# Revit family: Camera-Security-iPRO-Super_Dynamic-2MP_Vandal_Resistant_Outdoor_PTZ-_Network-WV-U65300-ZYX
name_source: partatom
category: Security Devices
units: mm (PartAtom-declared; Revit-internal decimal feet)

## family parameters
Cut with Voids When Loaded = No
Host = Face
Maintain Annotation Orientation = No
OmniClass Number = 23.85.10.14.11
OmniClass Title = Cameras
Part Type = Normal
Room Calculation Point = No
Round Connector Dimension = Use Diameter
Shared = No

## types (1)
- WV-U65300-ZY
    Alarm Input Or Output Specification = ALARM IN 1 (Alarm input 1/ Black & white input/ Auto time adjustment input) (x1) ALARM IN 2 (Alarm input 2/ ALARM OUT) (x1), ALARM IN 3 (Alarm input 3/ AUX OUT) (x1)
    Angle Of View = 113
    Audio In = Yes
    Audio Out = Yes
    Communication Ports = 10Base-T / 100Base-TX, RJ45 connector
    Date Last Modified = 2022/08/10
    Day Or Night = Yes
    Default Elevation = 0 "
    Description = Security Camera, 2MP 3.1x Outdoor PTZ Network Camera, WV-U65300-ZY
    Diameter = 6.102 "
    Equipment Abbreviation = SC
    Family Version = 1.0.0
    HFOV Max 169 = 113.00°
    HFOV Max 43 = 82.00°
    HFOV Min 169 = 36.00°
    HFOV Min 43 = 26.00°
    Has POE = Yes
    Height = 5.276 "
    IP Or Analog = IP
    Indoor Or Outdoor = Outdoor
    Manufacturer = i-PRO Co., Ltd.
    Minimum Illumination = 0.010 lx
    Model = WV-U65300-ZY
    Model Disclaimer = Contact i-PRO for more information
    Mounting Positions = Mount Dependent or Surface Mount
    Operational Humidity = 10 to 100 % (no condensation)
    Operational Temperature = -30 °C to +55 °C (-22 °F to +131 °F)
    Pan Max = 350.00°
    Pan Min = 0.00°
    Panning Range = 0 to +350°
    Part Description = Security Camera, 2MP 3.1x Outdoor PTZ Network Camera, WV-U65300-ZY
    Part Number = WV-U65300-ZY
    Product Documentation Link = https://bizpartner.panasonic.net
    Product Material = Paint - i-Pro White
    Product Page URL = https://i-pro.com
    Provide Feedback = https://i-pro.com
    Regulatory Compliance = UL (UL62368-1), c-UL (CSA C22.2 No.62368-1), CE, IEC62368-1, FCC (Part15 ClassA), ICES-003 Issue 7 ClassA, EN55032 ClassA, EN55035
    Shock Resistance = IK10 (IEC 62262)
    Storage Temperature = -30 °C to +55 °C (-22 °F to +131 °F)
    Super Dynamic Range = Yes
    Tilt Max = 90.00°
    Tilt Min = 0.00°
    Tilting Range = -30 to +90°
    URL = https://i-pro.com
    VFOV Max 169 = 60.00°
    VFOV Max 43 = 60.00°
    VFOV Min 169 = 20.00°
    VFOV Min 43 = 20.00°
    Vandal Resistant = Yes
    Water and Dust Resistance = IP66, IEC60529 measuring standard compatible, Type 4X(UL50E), NEMA 4X compliant
    Wide Dynamic Range = Yes
    Yaw Max = 0.00°
    Yaw Min = 0.00°
    Yawing Range = ±0°
    z Const Pan Handle Length = 19.488 "
    z Const Tilt Base Length = 9.843 "
    z Const Tilt Base2 Length = 19.685 "
    z Const Tilt Handle Length = 11.811 "
    z Const Yaw Base Length = 10.236 "
    z Const Yaw Base2 Length = 17.323 "
    z Const Yaw Handle Length = 9.252 "
    z VV Viewpoint Depth Max = 1.283 "
    z VV Viewpoint Depth Min = 1.283 "

## geometry (parser evidence)
native form markers: Blend x2, Sweep x7
no freeform markers — native parametric forms only
